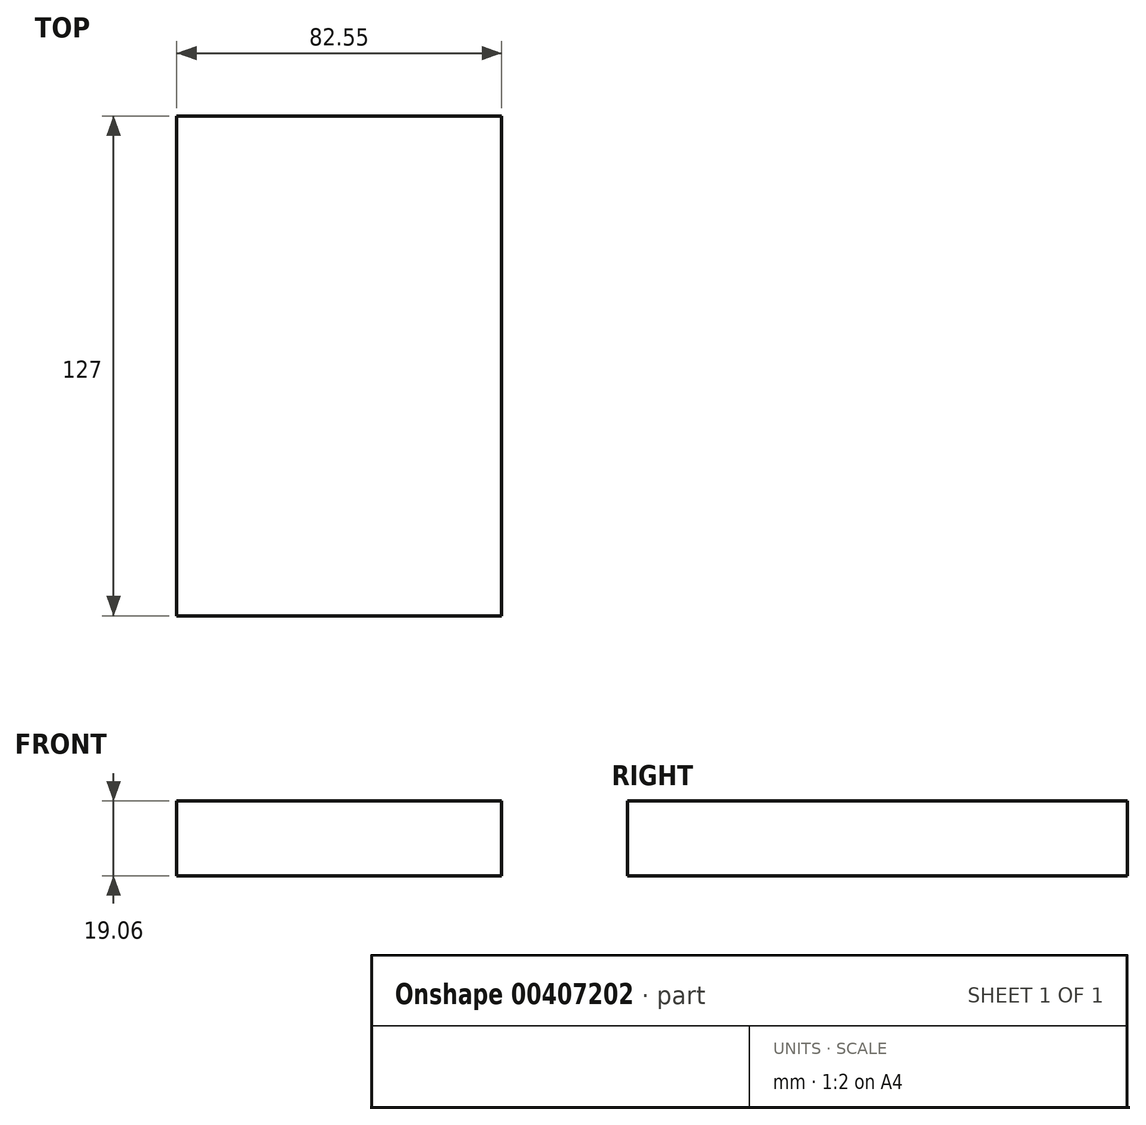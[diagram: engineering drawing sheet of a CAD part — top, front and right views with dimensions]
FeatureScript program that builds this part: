
annotation { "Feature Type Name" : "Feature", "Feature Type Description" : "" }
export const myFeature = defineFeature(function(context is Context, id is Id, definition is map)
    precondition{}
    {
        {
            var Q0;
            Q0=qCreatedBy(makeId("Front.planeOp"),FACE);
            var sketch = newSketch(context, id + "F0", { "sketchPlane" : qUnion([Q0])});
            skLineSegment(sketch, "E0.bottom", {"start": v(41.28, -9.52) * mm, "end": v(-41.28, -9.53) * mm});
            skLineSegment(sketch, "E0.top", {"start": v(41.28, 9.53) * mm, "end": v(-41.28, 9.53) * mm});
            skLineSegment(sketch, "E0.left", {"start": v(41.28, -9.52) * mm, "end": v(41.28, 9.53) * mm});
            skLineSegment(sketch, "E0.right", {"start": v(-41.28, -9.53) * mm, "end": v(-41.28, 9.53) * mm});
            skPoint(sketch, "E0.middle", {"position": v(0, 0) * mm});
            skLineSegment(sketch, "E1.bottom", {"start": v(99.5, 38.1) * mm, "end": v(48.7, 38.1) * mm});
            skLineSegment(sketch, "E1.top", {"start": v(99.5, 66.68) * mm, "end": v(48.7, 66.68) * mm});
            skLineSegment(sketch, "E1.left", {"start": v(99.5, 38.1) * mm, "end": v(99.5, 66.68) * mm});
            skLineSegment(sketch, "E1.right", {"start": v(48.7, 38.1) * mm, "end": v(48.7, 66.68) * mm});
            skPoint(sketch, "E1.middle", {"position": v(74.1, 52.39) * mm});
            skLineSegment(sketch, "E2", {"start": v(41.28, 9.53) * mm, "end": v(41.28, 40.4) * mm});
            skArc(sketch, "E3", {"start": v(41.28, 40.4) * mm, "mid": v(43.24, 48.54) * mm, "end": v(48.71, 54.88) * mm});
            skLineSegment(sketch, "E4", {"start": v(48.71, 54.88) * mm, "end": v(87.12, 54.88) * mm});
            skLineSegment(sketch, "E5.0", {"start": v(43.76, 73.93) * mm, "end": v(87.12, 73.93) * mm});
            skArc(sketch, "E5.1", {"start": v(22.23, 40.4) * mm, "mid": v(28.07, 60.32) * mm, "end": v(43.76, 73.93) * mm});
            skLineSegment(sketch, "E5.2", {"start": v(22.22, 9.53) * mm, "end": v(22.22, 40.4) * mm});
            skLineSegment(sketch, "E6", {"start": v(87.12, 54.88) * mm, "end": v(87.12, 73.93) * mm});
            skSolve(sketch);
        }
        {
            var Q0;
            Q0=makeQuery(id+"F0.imprint","IMPRINT",FACE,{"disambiguationData":[TD([[makeQuery(id+"F0.imprint","IMPRINT",EDGE,{"derivedFrom":sQuery(id+"F0.wireOp",EDGE,"E0.bottom")}),-1.0]])]});
            extrude(context, id + "F1", {"entities" : qUnion([Q0]), "endBound" : BoundingType.SYMMETRIC, "depth" : 127 * mm});
        }
    });
